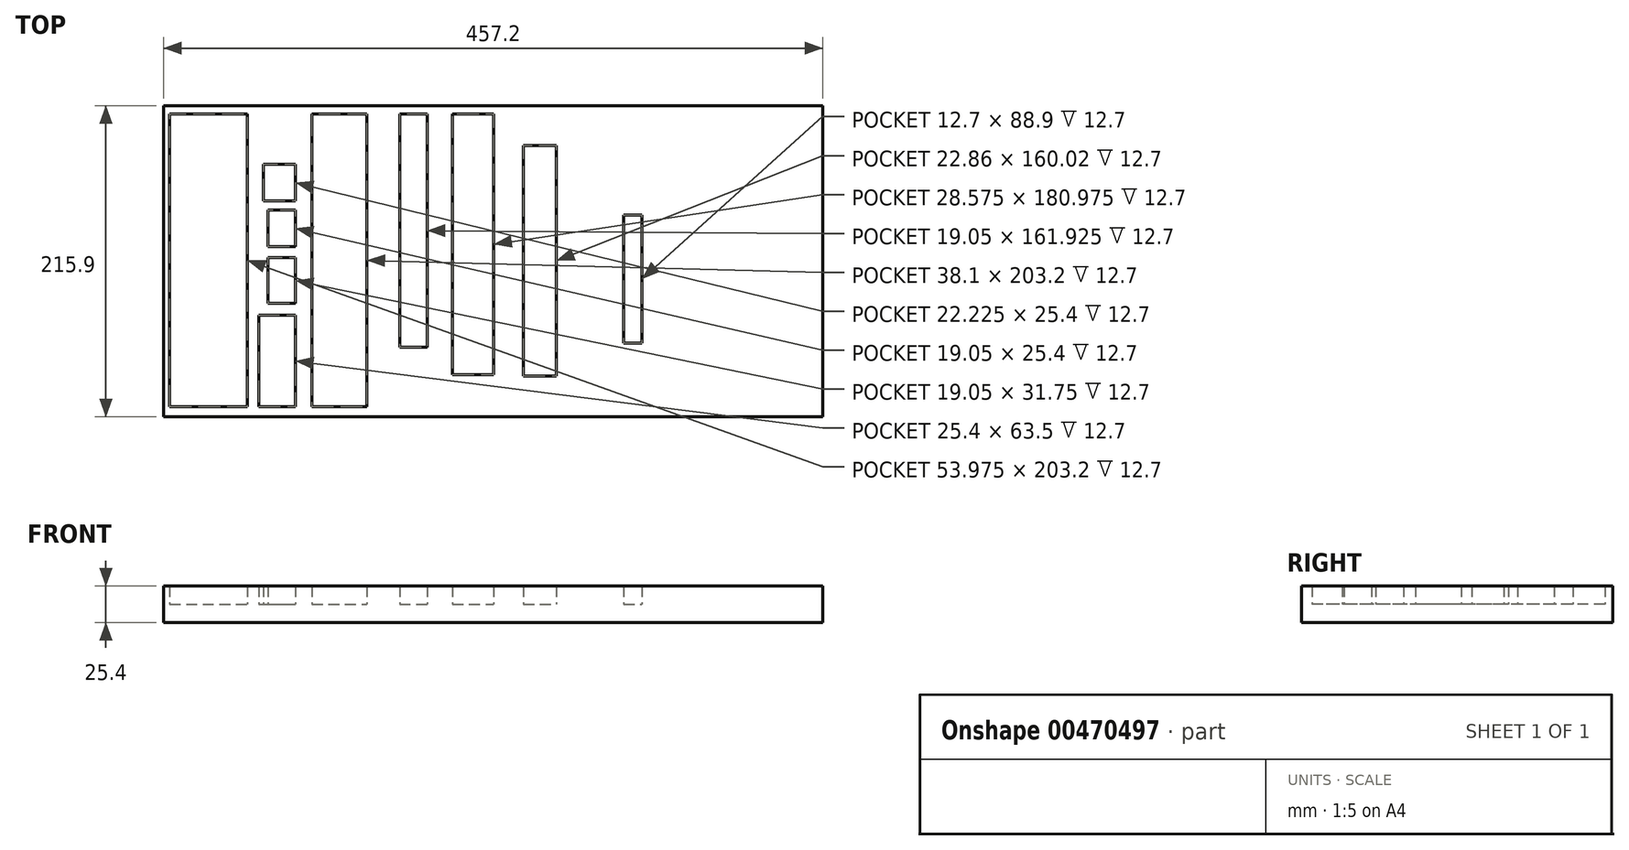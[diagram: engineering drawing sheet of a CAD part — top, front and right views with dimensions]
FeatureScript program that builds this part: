
annotation { "Feature Type Name" : "Feature", "Feature Type Description" : "" }
export const myFeature = defineFeature(function(context is Context, id is Id, definition is map)
    precondition{}
    {
        {
            var Q0;
            Q0=qCreatedBy(makeId("Top.planeOp"),FACE);
            var sketch = newSketch(context, id + "F0", { "sketchPlane" : qUnion([Q0])});
            skLineSegment(sketch, "E0.bottom", {"start": v(-182.77, 106.83) * mm, "end": v(274.43, 106.83) * mm});
            skLineSegment(sketch, "E0.top", {"start": v(-182.77, -109.07) * mm, "end": v(274.43, -109.07) * mm});
            skLineSegment(sketch, "E0.left", {"start": v(-182.77, 106.83) * mm, "end": v(-182.77, -109.07) * mm});
            skLineSegment(sketch, "E0.right", {"start": v(274.43, 106.83) * mm, "end": v(274.43, -109.07) * mm});
            skLineSegment(sketch, "E1.bottom", {"start": v(-178.52, 101.19) * mm, "end": v(-124.55, 101.19) * mm});
            skLineSegment(sketch, "E1.top", {"start": v(-178.52, -102.01) * mm, "end": v(-124.55, -102.01) * mm});
            skLineSegment(sketch, "E1.left", {"start": v(-178.52, 101.19) * mm, "end": v(-178.52, -102.01) * mm});
            skLineSegment(sketch, "E1.right", {"start": v(-124.55, 101.19) * mm, "end": v(-124.55, -102.01) * mm});
            skLineSegment(sketch, "E2.bottom", {"start": v(-116.81, -38.51) * mm, "end": v(-91.41, -38.51) * mm});
            skLineSegment(sketch, "E2.top", {"start": v(-116.81, -102.01) * mm, "end": v(-91.41, -102.01) * mm});
            skLineSegment(sketch, "E2.left", {"start": v(-116.81, -38.51) * mm, "end": v(-116.81, -102.01) * mm});
            skLineSegment(sketch, "E2.right", {"start": v(-91.41, -38.51) * mm, "end": v(-91.41, -102.01) * mm});
            skLineSegment(sketch, "E3.bottom", {"start": v(-110.46, 1.51) * mm, "end": v(-91.41, 1.51) * mm});
            skLineSegment(sketch, "E3.top", {"start": v(-110.46, -30.24) * mm, "end": v(-91.41, -30.24) * mm});
            skLineSegment(sketch, "E3.left", {"start": v(-110.46, 1.51) * mm, "end": v(-110.46, -30.24) * mm});
            skLineSegment(sketch, "E3.right", {"start": v(-91.41, 1.51) * mm, "end": v(-91.41, -30.24) * mm});
            skLineSegment(sketch, "E4.bottom", {"start": v(-110.46, 34.38) * mm, "end": v(-91.41, 34.38) * mm});
            skLineSegment(sketch, "E4.top", {"start": v(-110.46, 8.98) * mm, "end": v(-91.41, 8.98) * mm});
            skLineSegment(sketch, "E4.left", {"start": v(-110.46, 34.38) * mm, "end": v(-110.46, 8.98) * mm});
            skLineSegment(sketch, "E4.right", {"start": v(-91.41, 34.38) * mm, "end": v(-91.41, 8.98) * mm});
            skPoint(sketch, "E5.oppositeSnap0", {"position": v(-91.41, 21.68) * mm});
            skLineSegment(sketch, "E5.bottom", {"start": v(-113.64, 66.1) * mm, "end": v(-91.41, 66.1) * mm});
            skLineSegment(sketch, "E5.top", {"start": v(-113.64, 40.7) * mm, "end": v(-91.41, 40.7) * mm});
            skLineSegment(sketch, "E5.left", {"start": v(-113.64, 66.1) * mm, "end": v(-113.64, 40.7) * mm});
            skLineSegment(sketch, "E5.right", {"start": v(-91.41, 66.1) * mm, "end": v(-91.41, 40.7) * mm});
            skLineSegment(sketch, "E6.bottom", {"start": v(-79.9, 101.19) * mm, "end": v(-41.8, 101.19) * mm});
            skLineSegment(sketch, "E6.top", {"start": v(-79.9, -102.01) * mm, "end": v(-41.8, -102.01) * mm});
            skLineSegment(sketch, "E6.left", {"start": v(-79.9, 101.19) * mm, "end": v(-79.9, -102.01) * mm});
            skLineSegment(sketch, "E6.right", {"start": v(-41.8, 101.19) * mm, "end": v(-41.8, -102.01) * mm});
            skLineSegment(sketch, "E7.bottom", {"start": v(-19.05, 101.19) * mm, "end": v(0, 101.19) * mm});
            skLineSegment(sketch, "E7.top", {"start": v(-19.05, -60.74) * mm, "end": v(0, -60.74) * mm});
            skLineSegment(sketch, "E7.left", {"start": v(-19.05, 101.19) * mm, "end": v(-19.05, -60.74) * mm});
            skLineSegment(sketch, "E7.right", {"start": v(0, 101.19) * mm, "end": v(0, -60.74) * mm});
            skLineSegment(sketch, "E8.bottom", {"start": v(17.56, 101.19) * mm, "end": v(46.14, 101.19) * mm});
            skLineSegment(sketch, "E8.top", {"start": v(17.56, -79.79) * mm, "end": v(46.14, -79.79) * mm});
            skLineSegment(sketch, "E8.left", {"start": v(17.56, 101.19) * mm, "end": v(17.56, -79.79) * mm});
            skLineSegment(sketch, "E8.right", {"start": v(46.14, 101.19) * mm, "end": v(46.14, -79.79) * mm});
            skLineSegment(sketch, "E9.bottom", {"start": v(66.8, 79.03) * mm, "end": v(89.65, 79.03) * mm});
            skLineSegment(sketch, "E9.top", {"start": v(66.8, -80.99) * mm, "end": v(89.65, -80.99) * mm});
            skLineSegment(sketch, "E9.left", {"start": v(66.8, 79.03) * mm, "end": v(66.8, -80.99) * mm});
            skLineSegment(sketch, "E9.right", {"start": v(89.65, 79.03) * mm, "end": v(89.65, -80.99) * mm});
            skLineSegment(sketch, "E10.bottom", {"start": v(136.35, 30.98) * mm, "end": v(149.05, 30.98) * mm});
            skLineSegment(sketch, "E10.top", {"start": v(136.35, -57.92) * mm, "end": v(149.05, -57.92) * mm});
            skLineSegment(sketch, "E10.left", {"start": v(136.35, 30.98) * mm, "end": v(136.35, -57.92) * mm});
            skLineSegment(sketch, "E10.right", {"start": v(149.05, 30.98) * mm, "end": v(149.05, -57.92) * mm});
            skSolve(sketch);
        }
        {
            var Q0;
            Q0=makeQuery(id+"F0.imprint","IMPRINT",FACE,{"disambiguationData":[TD([[makeQuery(id+"F0.imprint","IMPRINT",EDGE,{"derivedFrom":sQuery(id+"F0.wireOp",EDGE,"E0.bottom")}),-1.0]])]});
            extrude(context, id + "F1", {"entities" : qUnion([Q0]), "depth" : 12.7 * mm});
        }
        {
            var Q0;
            Q0=makeQuery(id+"F1.opExtrude","CAP_FACE",FACE,{"disambiguationData":[OSD([sQuery(id+"F0.wireOp",EDGE,"E0.bottom"),sQuery(id+"F0.wireOp",EDGE,"E0.top"),sQuery(id+"F0.wireOp",EDGE,"E0.left"),sQuery(id+"F0.wireOp",EDGE,"E0.right"),sQuery(id+"F0.wireOp",EDGE,"E1.bottom"),sQuery(id+"F0.wireOp",EDGE,"E1.top"),sQuery(id+"F0.wireOp",EDGE,"E1.left"),sQuery(id+"F0.wireOp",EDGE,"E1.right"),sQuery(id+"F0.wireOp",EDGE,"E2.bottom"),sQuery(id+"F0.wireOp",EDGE,"E2.top"),sQuery(id+"F0.wireOp",EDGE,"E2.left"),sQuery(id+"F0.wireOp",EDGE,"E2.right"),sQuery(id+"F0.wireOp",EDGE,"E3.bottom"),sQuery(id+"F0.wireOp",EDGE,"E3.top"),sQuery(id+"F0.wireOp",EDGE,"E3.left"),sQuery(id+"F0.wireOp",EDGE,"E3.right"),sQuery(id+"F0.wireOp",EDGE,"E4.bottom"),sQuery(id+"F0.wireOp",EDGE,"E4.top"),sQuery(id+"F0.wireOp",EDGE,"E4.left"),sQuery(id+"F0.wireOp",EDGE,"E4.right"),sQuery(id+"F0.wireOp",EDGE,"E5.bottom"),sQuery(id+"F0.wireOp",EDGE,"E5.top"),sQuery(id+"F0.wireOp",EDGE,"E5.left"),sQuery(id+"F0.wireOp",EDGE,"E5.right"),sQuery(id+"F0.wireOp",EDGE,"E6.bottom"),sQuery(id+"F0.wireOp",EDGE,"E6.top"),sQuery(id+"F0.wireOp",EDGE,"E6.left"),sQuery(id+"F0.wireOp",EDGE,"E6.right"),sQuery(id+"F0.wireOp",EDGE,"E7.bottom"),sQuery(id+"F0.wireOp",EDGE,"E7.top"),sQuery(id+"F0.wireOp",EDGE,"E7.left"),sQuery(id+"F0.wireOp",EDGE,"E7.right"),sQuery(id+"F0.wireOp",EDGE,"E8.bottom"),sQuery(id+"F0.wireOp",EDGE,"E8.top"),sQuery(id+"F0.wireOp",EDGE,"E8.left"),sQuery(id+"F0.wireOp",EDGE,"E8.right"),sQuery(id+"F0.wireOp",EDGE,"E9.bottom"),sQuery(id+"F0.wireOp",EDGE,"E9.top"),sQuery(id+"F0.wireOp",EDGE,"E9.left"),sQuery(id+"F0.wireOp",EDGE,"E9.right"),sQuery(id+"F0.wireOp",EDGE,"E10.bottom"),sQuery(id+"F0.wireOp",EDGE,"E10.top"),sQuery(id+"F0.wireOp",EDGE,"E10.left"),sQuery(id+"F0.wireOp",EDGE,"E10.right")])],"isStart":true});
            var sketch = newSketch(context, id + "F2", { "sketchPlane" : qUnion([Q0])});
            skLineSegment(sketch, "E11.bottom", {"start": v(-182.77, 109.07) * mm, "end": v(274.43, 109.07) * mm});
            skLineSegment(sketch, "E11.top", {"start": v(-182.77, -106.83) * mm, "end": v(274.43, -106.83) * mm});
            skLineSegment(sketch, "E11.left", {"start": v(-182.77, 109.07) * mm, "end": v(-182.77, -106.83) * mm});
            skLineSegment(sketch, "E11.right", {"start": v(274.43, 109.07) * mm, "end": v(274.43, -106.83) * mm});
            skSolve(sketch);
        }
        {
            var Q0;
            Q0 = qSketchRegion(id + "F2", true);
            extrude(context, id + "F3", {"entities" : qUnion([Q0]), "operationType" : NewBodyOperationType.ADD, "depth" : 12.7 * mm});
        }
    });
